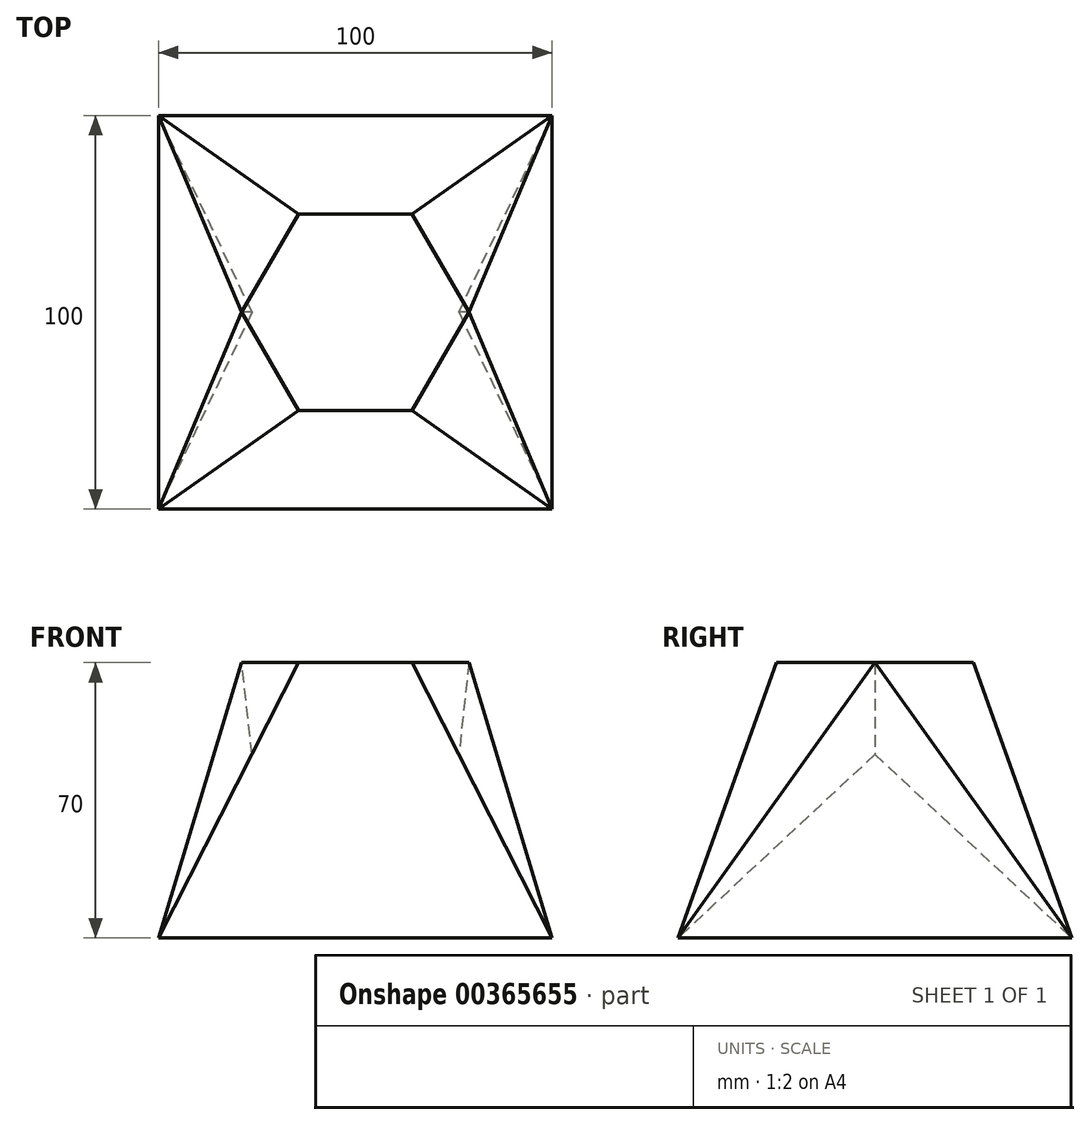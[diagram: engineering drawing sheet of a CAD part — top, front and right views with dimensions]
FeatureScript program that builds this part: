
annotation { "Feature Type Name" : "Feature", "Feature Type Description" : "" }
export const myFeature = defineFeature(function(context is Context, id is Id, definition is map)
    precondition{}
    {
        {
            var Q0;
            Q0=qCreatedBy(makeId("Top.planeOp"),FACE);
            var sketch = newSketch(context, id + "F0", { "sketchPlane" : qUnion([Q0])});
            skLineSegment(sketch, "E0.bottom", {"start": v(50, 50) * mm, "end": v(-50, 50) * mm});
            skLineSegment(sketch, "E0.top", {"start": v(50, -50) * mm, "end": v(-50, -50) * mm});
            skLineSegment(sketch, "E0.left", {"start": v(50, 50) * mm, "end": v(50, -50) * mm});
            skLineSegment(sketch, "E0.right", {"start": v(-50, 50) * mm, "end": v(-50, -50) * mm});
            skPoint(sketch, "E0.middle", {"position": v(0, 0) * mm});
            skSolve(sketch);
        }
        {
            var Q0;
            Q0=qCreatedBy(makeId("Top.planeOp"),FACE);
            cPlane(context, id + "F1", {"entities" : qUnion([Q0]), "cplaneType" : CPlaneType.OFFSET, "offset" : 70 * mm, "width" : 150 * mm, "height" : 150 * mm});
        }
        {
            var Q0;
            Q0=qCreatedBy(id+"F1.planeOp",FACE);
            var sketch = newSketch(context, id + "F2", { "sketchPlane" : qUnion([Q0])});
            skCircle(sketch, "E1.cCircle", {"center": v(0, 0) * mm, "radius": 25 * mm, "construction": true});
            skLineSegment(sketch, "E1.0", {"start": v(-14.43, 25) * mm, "end": v(14.43, 25) * mm});
            skLineSegment(sketch, "E1.1", {"start": v(14.43, 25) * mm, "end": v(28.87, 0) * mm});
            skLineSegment(sketch, "E1.2", {"start": v(28.87, 0) * mm, "end": v(14.43, -25) * mm});
            skLineSegment(sketch, "E1.3", {"start": v(14.43, -25) * mm, "end": v(-14.43, -25) * mm});
            skLineSegment(sketch, "E1.4", {"start": v(-14.43, -25) * mm, "end": v(-28.87, 0) * mm});
            skLineSegment(sketch, "E1.5", {"start": v(-28.87, 0) * mm, "end": v(-14.43, 25) * mm});
            skPoint(sketch, "E1.0.midPoint", {"position": v(0, 25) * mm});
            skLineSegment(sketch, "E2", {"start": v(-14.43, 25) * mm, "end": v(-14.43, -25) * mm});
            skLineSegment(sketch, "E3", {"start": v(14.43, 25) * mm, "end": v(14.43, -25) * mm});
            skSolve(sketch);
        }
        {
            var Q0;
            Q0=makeQuery(id+"F0.imprint","IMPRINT",FACE,{"disambiguationData":[TD([[makeQuery(id+"F0.imprint","IMPRINT",EDGE,{"derivedFrom":sQuery(id+"F0.wireOp",EDGE,"E0.bottom")}),1.0]])]});
            var Q1;
            Q1=makeQuery(id+"F2.imprint","IMPRINT",FACE,{"disambiguationData":[TD([[makeQuery(id+"F2.imprint","IMPRINT",EDGE,{"derivedFrom":sQuery(id+"F2.wireOp",EDGE,"E1.0")}),-1.0]])]});
            loft(context, id + "F3", {"sheetProfilesArray" : [{ "sheetProfileEntities" : qUnion([Q0]) }, { "sheetProfileEntities" : qUnion([Q1]) }]});
        }
        {
            var Q1;
            Q1=makeQuery(id+"F2.imprint","IMPRINT",FACE,{"disambiguationData":[TD([[makeQuery(id+"F2.imprint","IMPRINT",EDGE,{"derivedFrom":sQuery(id+"F2.wireOp",EDGE,"E1.4")}),-1.0]])]});
            var Q2;
            Q2=sQuery(id+"F0.wireOp",VERTEX,"E0.right.end");
            loft(context, id + "F4", {"operationType" : NewBodyOperationType.ADD, "sheetProfilesArray" : [{ "sheetProfileEntities" : qUnion([Q1]) }, { "sheetProfileEntities" : qUnion([Q2]) }]});
        }
        {
            var Q1;
            Q1=makeQuery(id+"F2.imprint","IMPRINT",FACE,{"disambiguationData":[TD([[makeQuery(id+"F2.imprint","IMPRINT",EDGE,{"derivedFrom":sQuery(id+"F2.wireOp",EDGE,"E1.4")}),-1.0]])]});
            var Q2;
            Q2=sQuery(id+"F0.wireOp",VERTEX,"E0.right.start");
            loft(context, id + "F5", {"operationType" : NewBodyOperationType.ADD, "sheetProfilesArray" : [{ "sheetProfileEntities" : qUnion([Q1]) }, { "sheetProfileEntities" : qUnion([Q2]) }]});
        }
        {
            var Q1;
            Q1=makeQuery(id+"F5.opLoft","SWEPT_FACE",FACE,{"disambiguationData":[OSD([sQuery(id+"F2.wireOp",EDGE,"E1.3"),sQuery(id+"F2.wireOp",EDGE,"E1.4"),sQuery(id+"F2.wireOp",EDGE,"E1.5"),sQuery(id+"F2.wireOp",EDGE,"E2")])]});
            var Q2;
            Q2=makeQuery(id+"F4.opLoft","SWEPT_FACE",FACE,{"disambiguationData":[OSD([sQuery(id+"F2.wireOp",EDGE,"E1.0"),sQuery(id+"F2.wireOp",EDGE,"E1.4"),sQuery(id+"F2.wireOp",EDGE,"E1.5"),sQuery(id+"F2.wireOp",EDGE,"E2")])]});
            var Q3;
            Q3=makeQuery(id+"F3.opLoft","MID_CAP_EDGE",EDGE,{"disambiguationData":[OSD([sQuery(id+"F0.wireOp",EDGE,"E0.bottom"),sQuery(id+"F0.wireOp",EDGE,"E0.top"),sQuery(id+"F0.wireOp",EDGE,"E0.right")])],"capPos":0.0});
            loft(context, id + "F6", {"addGuides" : true, "sheetProfilesArray" : [{ "sheetProfileEntities" : qUnion([Q1]) }, { "sheetProfileEntities" : qUnion([Q2]) }], "guidesArray" : [{ "guideEntities" : qUnion([Q3]), "guideDerivativeType" : LoftGuideDerivativeType.DEFAULT, "guideDerivativeMagnitude" : 1 }]});
        }
        {
            var Q1;
            Q1=makeQuery(id+"F2.imprint","IMPRINT",FACE,{"disambiguationData":[TD([[makeQuery(id+"F2.imprint","IMPRINT",EDGE,{"derivedFrom":sQuery(id+"F2.wireOp",EDGE,"E1.1")}),-1.0]])]});
            var Q2;
            Q2=makeQuery(id+"F3.opLoft","MID_CAP_VERTEX",VERTEX,{"disambiguationData":[OSD([sQuery(id+"F0.wireOp",EDGE,"E0.top"),sQuery(id+"F0.wireOp",EDGE,"E0.left")])],"capPos":0.0});
            loft(context, id + "F7", {"operationType" : NewBodyOperationType.ADD, "sheetProfilesArray" : [{ "sheetProfileEntities" : qUnion([Q1]) }, { "sheetProfileEntities" : qUnion([Q2]) }]});
        }
        {
            var Q1;
            Q1=makeQuery(id+"F2.imprint","IMPRINT",FACE,{"disambiguationData":[TD([[makeQuery(id+"F2.imprint","IMPRINT",EDGE,{"derivedFrom":sQuery(id+"F2.wireOp",EDGE,"E1.1")}),-1.0]])]});
            var Q2;
            Q2=makeQuery(id+"F3.opLoft","MID_CAP_VERTEX",VERTEX,{"disambiguationData":[OSD([sQuery(id+"F0.wireOp",EDGE,"E0.bottom"),sQuery(id+"F0.wireOp",EDGE,"E0.left")])],"capPos":0.0});
            loft(context, id + "F8", {"operationType" : NewBodyOperationType.ADD, "sheetProfilesArray" : [{ "sheetProfileEntities" : qUnion([Q1]) }, { "sheetProfileEntities" : qUnion([Q2]) }]});
        }
        {
            var Q1;
            Q1=makeQuery(id+"F7.opLoft","SWEPT_FACE",FACE,{"disambiguationData":[OSD([sQuery(id+"F2.wireOp",EDGE,"E1.0"),sQuery(id+"F2.wireOp",EDGE,"E1.1"),sQuery(id+"F2.wireOp",EDGE,"E1.2"),sQuery(id+"F2.wireOp",EDGE,"E3")])]});
            var Q2;
            Q2=makeQuery(id+"F8.opLoft","SWEPT_FACE",FACE,{"disambiguationData":[OSD([sQuery(id+"F2.wireOp",EDGE,"E1.1"),sQuery(id+"F2.wireOp",EDGE,"E1.2"),sQuery(id+"F2.wireOp",EDGE,"E1.3"),sQuery(id+"F2.wireOp",EDGE,"E3")])]});
            var Q3;
            Q3=makeQuery(id+"F3.opLoft","MID_CAP_EDGE",EDGE,{"disambiguationData":[OSD([sQuery(id+"F0.wireOp",EDGE,"E0.bottom"),sQuery(id+"F0.wireOp",EDGE,"E0.top"),sQuery(id+"F0.wireOp",EDGE,"E0.left")])],"capPos":0.0});
            loft(context, id + "F9", {"addGuides" : true, "sheetProfilesArray" : [{ "sheetProfileEntities" : qUnion([Q1]) }, { "sheetProfileEntities" : qUnion([Q2]) }], "guidesArray" : [{ "guideEntities" : qUnion([Q3]), "guideDerivativeType" : LoftGuideDerivativeType.DEFAULT, "guideDerivativeMagnitude" : 1 }]});
        }
    });
